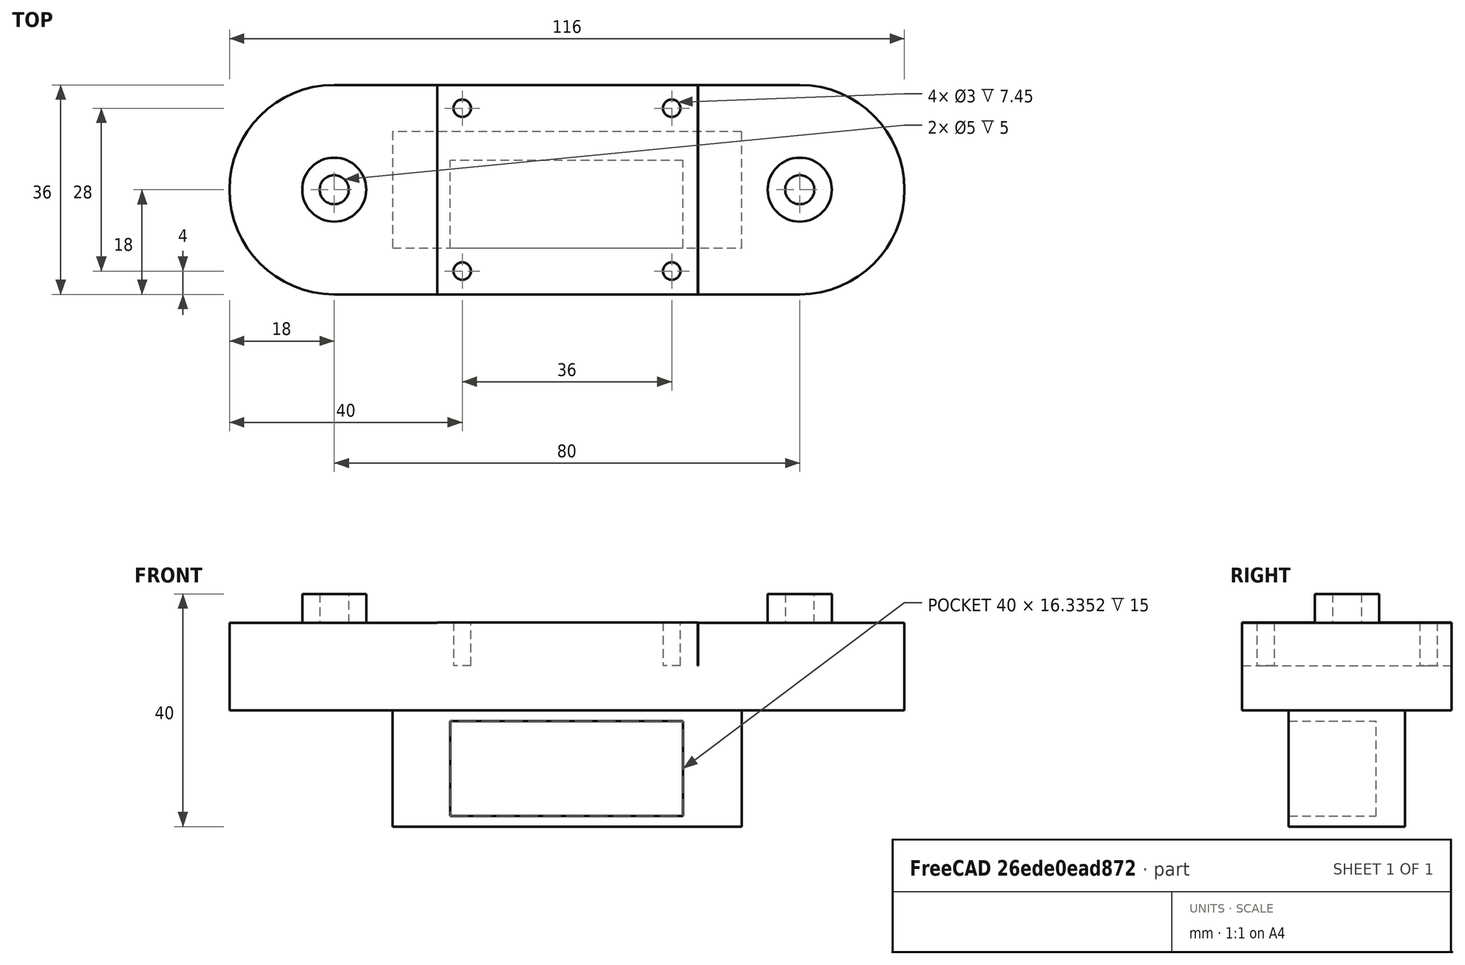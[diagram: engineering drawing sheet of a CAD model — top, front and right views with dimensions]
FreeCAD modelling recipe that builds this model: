
FCSTD DOCUMENT  (FreeCAD 0.19R24267 +148 (Git))
Label: Table
License: All rights reserved
LicenseURL: http://en.wikipedia.org/wiki/All_rights_reserved
objects: TechDraw::DrawViewDimension×64, Sketcher::SketchObject×7, PartDesign::Plane×5, TechDraw::DrawViewPart×5, PartDesign::Pad×4, PartDesign::Pocket×2, Part::Part2DObjectPython×1, PartDesign::Body×1, TechDraw::DrawSVGTemplate×1, TechDraw::DrawPage×1
note: 26 computed .brp shape members not serialized (recipe doc carries the construction recipe); baked Part::Feature solids carry a one-line shape summary decoded from their .brp

FEATURE [Sketcher::SketchObject] Sketch
  FullyConstrained = false
  MapMode = 5
  Support = -> [XY_Plane]
  sketch-geometry (16):
    g0: LineSegment StartX=-40 StartY=18 StartZ=0 EndX=40 EndY=18 EndZ=0
    g1: LineSegment StartX=40 StartY=-18 StartZ=0 EndX=-40 EndY=-18 EndZ=0
    g2: ArcOfCircle CenterX=-40 CenterY=-4.82e-14 CenterZ=0 NormalX=0 NormalY=0 NormalZ=1 AngleXU=0 Radius=18 StartAngle=1.5708 EndAngle=4.71239
    g3: ArcOfCircle CenterX=40 CenterY=-4.71e-14 CenterZ=0 NormalX=0 NormalY=0 NormalZ=1 AngleXU=0 Radius=18 StartAngle=4.71239 EndAngle=7.85398
    g4: LineSegment StartX=22.5 StartY=-18 StartZ=0 EndX=-22.5 EndY=-18 EndZ=0
    g5: LineSegment StartX=-22.5 StartY=-18 StartZ=0 EndX=-22.5 EndY=18 EndZ=0
    g6: LineSegment StartX=-22.5 StartY=18 StartZ=0 EndX=22.5 EndY=18 EndZ=0
    g7: LineSegment StartX=22.5 StartY=18 StartZ=0 EndX=22.5 EndY=-18 EndZ=0
    g8: Circle CenterX=-40 CenterY=-4.82e-14 CenterZ=0 NormalX=0 NormalY=0 NormalZ=1 AngleXU=0 Radius=10
    g9: Circle CenterX=40 CenterY=-4.71e-14 CenterZ=0 NormalX=0 NormalY=0 NormalZ=1 AngleXU=0 Radius=10
    g10: Circle CenterX=40 CenterY=-4.71e-14 CenterZ=0 NormalX=0 NormalY=0 NormalZ=1 AngleXU=0 Radius=5.5
    g11: Circle CenterX=-40 CenterY=-4.82e-14 CenterZ=0 NormalX=0 NormalY=0 NormalZ=1 AngleXU=0 Radius=5.5
    g12: Circle CenterX=-18 CenterY=14 CenterZ=0 NormalX=0 NormalY=0 NormalZ=1 AngleXU=0 Radius=1.5
    g13: Circle CenterX=18 CenterY=14 CenterZ=0 NormalX=0 NormalY=0 NormalZ=1 AngleXU=0 Radius=1.5
    g14: Circle CenterX=-18 CenterY=-14 CenterZ=0 NormalX=0 NormalY=0 NormalZ=1 AngleXU=0 Radius=1.5
    g15: Circle CenterX=18 CenterY=-14 CenterZ=0 NormalX=0 NormalY=0 NormalZ=1 AngleXU=0 Radius=1.5
  constraints (39):
    c: Horizontal(g0)
    c: Horizontal(g1)
    c: Symmetric(g0,g1,g-1)
    c: DistanceX(g0,g0) = 80
    c: Coincident(g4,g5)
    c: Coincident(g5,g6)
    c: Coincident(g6,g7)
    c: Coincident(g7,g4)
    c: Horizontal(g4)
    c: Horizontal(g6)
    c: Vertical(g5)
    c: Vertical(g7)
    c: PointOnObject(g4,g1)
    c: DistanceX(g5,g6) = 45
    c: Tangent(g2,g0) = 1.5708
    c: Symmetric(g5,g4,g-1)
    c: Coincident(g8,g2)
    c: Coincident(g9,g3)
    c: Coincident(g10,g3)
    c: Coincident(g11,g2)
    c: Diameter(g9) = 20
    c: Diameter(g10) = 11
    c: Diameter(g11) = 11
    c: Diameter(g8) = 20
    c: Tangent(g3,g0) = 1.5708
    c: Tangent(g1,g3)
    c: Tangent(g2,g1) = 1.5708
    c: Radius(g3) = 18
    c: Symmetric(g15,g12,g-1)
    c: DistanceX(g12,g13) = 36
    c: Equal(g13,g15)
    c: Diameter(g13) = 3
    c: Equal(g12,g14)
    c: Diameter(g12) = 3
    c: Vertical(g14,g12)
    c: Horizontal(g15,g14)
    c: Vertical(g13,g15)
    c: Horizontal(g13,g12)
    c: DistanceY(g14,g12) = 28
FEATURE [Sketcher::SketchObject] Sketch001  label="Top"
  ExternalGeometry = -> [Sketch]
  FullyConstrained = true
  MapMode = 5
  Support = -> [XY_Plane]
  sketch-geometry (4):
    g0: ArcOfCircle CenterX=-40 CenterY=0 CenterZ=0 NormalX=0 NormalY=0 NormalZ=1 AngleXU=0 Radius=18 StartAngle=1.5708 EndAngle=4.71239
    g1: ArcOfCircle CenterX=40 CenterY=0 CenterZ=0 NormalX=0 NormalY=0 NormalZ=1 AngleXU=0 Radius=18 StartAngle=4.71239 EndAngle=7.85398
    g2: LineSegment StartX=-40 StartY=18 StartZ=0 EndX=40 EndY=18 EndZ=0
    g3: LineSegment StartX=40 StartY=-18 StartZ=0 EndX=-40 EndY=-18 EndZ=0
  constraints (11):
    c: Coincident(g0,g-4)
    c: Coincident(g1,g-6)
    c: PointOnObject(g-6,g1)
    c: Coincident(g2,g-4)
    c: Coincident(g2,g-6)
    c: Coincident(g3,g-6)
    c: Coincident(g3,g-5)
    c: Coincident(g0,g2)
    c: Coincident(g0,g3)
    c: Coincident(g1,g3)
    c: Coincident(g1,g2)
FEATURE [Part::Part2DObjectPython] Clone2D  label="Sketch (2D)"  # Draft 2D object (typed FeaturePython)
  Fuse = false
  Objects = -> [Sketch]
  Placement = pos=(0,0,16) rot=(0,0,1;0rad)
  Scale = (1,1,1)
FEATURE [PartDesign::Pad] Pad
  Direction = (1,1,1)
  Length = 15
  Length2 = 100
  Profile = -> Sketch001
  Type = 0
FEATURE [PartDesign::Plane] DatumPlane
  Length = 130.952
  MapMode = 5
  Placement = pos=(0,-18,0) rot=(1,0,0;1.5708rad)
  ResizeMode = 0
  Support = -> [Pad]
  Width = 65.2143
FEATURE [Sketcher::SketchObject] Sketch002
  FullyConstrained = false
  MapMode = 5
  Placement = pos=(0,-18,0) rot=(1,0,0;1.5708rad)
  Support = -> [DatumPlane]
  sketch-geometry (4):
    g0: LineSegment StartX=-22.3088 StartY=31.7993 StartZ=0 EndX=22.546 EndY=31.7993 EndZ=0
    g1: LineSegment StartX=22.546 StartY=31.7993 StartZ=0 EndX=22.546 EndY=7.65691 EndZ=0
    g2: LineSegment StartX=22.546 StartY=7.65691 StartZ=0 EndX=-22.3088 EndY=7.65691 EndZ=0
    g3: LineSegment StartX=-22.3088 StartY=7.65691 StartZ=0 EndX=-22.3088 EndY=31.7993 EndZ=0
  constraints (8):
    c: Coincident(g0,g1)
    c: Coincident(g1,g2)
    c: Coincident(g2,g3)
    c: Coincident(g3,g0)
    c: Horizontal(g0)
    c: Horizontal(g2)
    c: Vertical(g1)
    c: Vertical(g3)
FEATURE [PartDesign::Pocket] Pocket
  BaseFeature = -> Pad
  Length = 36
  Length2 = 100
  Profile = -> Sketch002
  Type = 0
FEATURE [Sketcher::SketchObject] Sketch003
  ExternalGeometry = -> [Clone2D,Pocket]
  FullyConstrained = false
  MapMode = 5
  Placement = pos=(0,1.7e-15,7.65691) rot=(0,0,1;0rad)
  Support = -> [Pocket]
  sketch-geometry (8):
    g0: LineSegment StartX=-22.3088 StartY=18 StartZ=0 EndX=22.5 EndY=18 EndZ=0
    g1: LineSegment StartX=22.5 StartY=18 StartZ=0 EndX=22.5 EndY=-18 EndZ=0
    g2: LineSegment StartX=22.5 StartY=-18 StartZ=0 EndX=-22.3088 EndY=-18 EndZ=0
    g3: LineSegment StartX=-22.3088 StartY=-18 StartZ=0 EndX=-22.3088 EndY=18 EndZ=0
    g4: Circle CenterX=-18 CenterY=14 CenterZ=0 NormalX=0 NormalY=0 NormalZ=1 AngleXU=0 Radius=1.5
    g5: Circle CenterX=18 CenterY=14 CenterZ=0 NormalX=0 NormalY=0 NormalZ=1 AngleXU=0 Radius=1.5
    g6: Circle CenterX=18 CenterY=-14 CenterZ=0 NormalX=0 NormalY=0 NormalZ=1 AngleXU=0 Radius=1.5
    g7: Circle CenterX=-18 CenterY=-14 CenterZ=0 NormalX=0 NormalY=0 NormalZ=1 AngleXU=0 Radius=1.5
  constraints (14):
    c: Coincident(g0,g1)
    c: Coincident(g1,g2)
    c: Coincident(g2,g3)
    c: Coincident(g3,g0)
    c: Horizontal(g0)
    c: Horizontal(g2)
    c: Vertical(g1)
    c: Vertical(g3)
    c: Coincident(g0,g-4)
    c: Coincident(g1,g-5)
    c: Coincident(g4,g-7)
    c: Coincident(g5,g-9)
    c: Coincident(g6,g-10)
    c: Coincident(g7,g-8)
FEATURE [PartDesign::Plane] DatumPlane001
  Length = 130.952
  MapMode = 5
  Placement = pos=(0,1.7e-15,7.65691) rot=(0,0,1;0rad)
  ResizeMode = 0
  Support = -> [Pocket]
  Width = 65.2143
FEATURE [PartDesign::Pad] Pad001  label="Surface"
  BaseFeature = -> Pocket
  Direction = (1,1,1)
  Length = 7.45
  Length2 = 100
  Profile = -> Sketch003
  Type = 0
FEATURE [PartDesign::Plane] DatumPlane002
  Length = 130.952
  MapMode = 5
  Placement = pos=(0,0,15) rot=(0,0,1;0rad)
  ResizeMode = 0
  Support = -> [Pad001]
  Width = 65.2143
FEATURE [Sketcher::SketchObject] Sketch004
  ExternalGeometry = -> [Clone2D]
  FullyConstrained = false
  MapMode = 5
  Placement = pos=(0,0,15) rot=(0,0,1;0rad)
  Support = -> [Pad001]
  sketch-geometry (4):
    g0: Circle CenterX=-40 CenterY=-4.82e-14 CenterZ=0 NormalX=0 NormalY=0 NormalZ=1 AngleXU=0 Radius=2.5
    g1: Circle CenterX=40 CenterY=-4.71e-14 CenterZ=0 NormalX=0 NormalY=0 NormalZ=1 AngleXU=0 Radius=2.5
    g2: Circle CenterX=-40 CenterY=-4.82e-14 CenterZ=0 NormalX=0 NormalY=0 NormalZ=1 AngleXU=0 Radius=5.5
    g3: Circle CenterX=40 CenterY=-4.71e-14 CenterZ=0 NormalX=0 NormalY=0 NormalZ=1 AngleXU=0 Radius=5.5
  constraints (6):
    c: Coincident(g0,g-4)
    c: Coincident(g1,g-3)
    c: Coincident(g2,g0)
    c: Tangent(g2,g-4)
    c: Coincident(g3,g1)
    c: Tangent(g3,g-3)
FEATURE [PartDesign::Pad] Pad002
  BaseFeature = -> Pad001
  Direction = (1,1,1)
  Length = 5
  Length2 = 100
  Profile = -> Sketch004
  Type = 0
FEATURE [PartDesign::Plane] DatumPlane003
  Length = 130.952
  MapMode = 5
  Placement = pos=(0,0,0) rot=(1,0,0;3.14159rad)
  ResizeMode = 0
  Support = -> [Pad002]
  Width = 65.2143
FEATURE [Sketcher::SketchObject] Sketch005
  FullyConstrained = true
  MapMode = 5
  Placement = pos=(0,0,0) rot=(1,0,0;3.14159rad)
  Support = -> [Pad002]
  sketch-geometry (4):
    g0: LineSegment StartX=-30 StartY=10 StartZ=0 EndX=30 EndY=10 EndZ=0
    g1: LineSegment StartX=30 StartY=10 StartZ=0 EndX=30 EndY=-10 EndZ=0
    g2: LineSegment StartX=30 StartY=-10 StartZ=0 EndX=-30 EndY=-10 EndZ=0
    g3: LineSegment StartX=-30 StartY=-10 StartZ=0 EndX=-30 EndY=10 EndZ=0
  constraints (11):
    c: Coincident(g0,g1)
    c: Coincident(g1,g2)
    c: Coincident(g2,g3)
    c: Coincident(g3,g0)
    c: Horizontal(g0)
    c: Horizontal(g2)
    c: Vertical(g1)
    c: Vertical(g3)
    c: Symmetric(g1,g0,g-1)
    c: DistanceX(g0,g0) = 60
    c: DistanceY(g3,g3) = 20
FEATURE [PartDesign::Pad] Pad003  label="Base"
  BaseFeature = -> Pad002
  Direction = (1,1,1)
  Length = 20
  Length2 = 100
  Profile = -> Sketch005
  Type = 0
FEATURE [PartDesign::Plane] DatumPlane004
  Length = 130.952
  MapMode = 5
  Placement = pos=(0,-10,0) rot=(1,0,0;1.5708rad)
  ResizeMode = 0
  Support = -> [Pad003]
  Width = 65.2143
FEATURE [Sketcher::SketchObject] Sketch006
  FullyConstrained = false
  MapMode = 5
  Placement = pos=(0,-10,0) rot=(1,0,0;1.5708rad)
  Support = -> [Pad003]
  sketch-geometry (4):
    g0: LineSegment StartX=-20.0443 StartY=-1.87066 StartZ=0 EndX=19.9557 EndY=-1.87066 EndZ=0
    g1: LineSegment StartX=19.9557 StartY=-1.87066 StartZ=0 EndX=19.9557 EndY=-18.2059 EndZ=0
    g2: LineSegment StartX=19.9557 StartY=-18.2059 StartZ=0 EndX=-20.0443 EndY=-18.2059 EndZ=0
    g3: LineSegment StartX=-20.0443 StartY=-18.2059 StartZ=0 EndX=-20.0443 EndY=-1.87066 EndZ=0
  constraints (9):
    c: Coincident(g0,g1)
    c: Coincident(g1,g2)
    c: Coincident(g2,g3)
    c: Coincident(g3,g0)
    c: Horizontal(g0)
    c: Horizontal(g2)
    c: Vertical(g1)
    c: Vertical(g3)
    c: DistanceX(g0,g0) = 40
FEATURE [PartDesign::Pocket] Pocket001  label="Foot area"
  BaseFeature = -> Pad003
  Length = 15
  Length2 = 100
  Profile = -> Sketch006
  Type = 0
FEATURE [PartDesign::Body] Body
  Group = -> [Sketch,Sketch001,Clone2D,Pad,DatumPlane,Sketch002,Pocket,Sketch003,DatumPlane001,Pad001,DatumPlane002,Sketch004,Pad002,DatumPlane003,Sketch005,Pad003,DatumPlane004,Sketch006,Pocket001]
  Origin = -> Origin
  Tip = -> Pocket001
FEATURE [TechDraw::DrawSVGTemplate] Template
  EditableTexts = AuthorName=AUTHOR NAME; CheckDate=CHECK DATE; CreationDate=CREATION DATE; DrawingNumber=NUMBER; FC-Scale=SCALE; FC-Title=TITLE; SheetNumber=SHEET; Subtitle=SUBTITLE; SupervisorName=SUPERVISOR NAME; Weight=WEIGHT
  Height = 297
  Orientation = 1
  Width = 420
FEATURE [TechDraw::DrawViewPart] View  label="TOP VIEW"
  CoarseView = false
  Direction = (0,0,1)
  Focus = 100
  HardHidden = false
  IsoCount = 0
  IsoHidden = false
  IsoVisible = false
  LockPosition = false
  Perspective = false
  Rotation = 0
  ScaleType = 0
  SeamHidden = false
  SeamVisible = true
  SmoothHidden = false
  SmoothVisible = true
  Source = -> [Pocket001]
  X = 106.209
  XDirection = (1,0,0)
  Y = 222.175
FEATURE [TechDraw::DrawViewPart] View002  label="SIDE VIEW"
  CoarseView = false
  Direction = (-1,0,0)
  Focus = 100
  HardHidden = false
  IsoCount = 0
  IsoHidden = false
  IsoVisible = false
  LockPosition = false
  Perspective = false
  Rotation = 0
  ScaleType = 0
  SeamHidden = false
  SeamVisible = true
  SmoothHidden = false
  SmoothVisible = true
  Source = -> [Pocket001]
  X = 116.97
  XDirection = (0,-1,0)
  Y = 51.7602
FEATURE [TechDraw::DrawViewPart] View004  label="FRONT VIEW"
  CoarseView = false
  Direction = (0,-1,0)
  Focus = 100
  HardHidden = false
  IsoCount = 0
  IsoHidden = false
  IsoVisible = false
  LockPosition = false
  Perspective = false
  Rotation = 0
  ScaleType = 0
  SeamHidden = false
  SeamVisible = true
  SmoothHidden = false
  SmoothVisible = true
  Source = -> [Pocket001]
  X = 310.217
  XDirection = (1,0,0)
  Y = 223.753
FEATURE [TechDraw::DrawViewPart] View005  label="REAR VIEW"
  CoarseView = false
  Direction = (0,1,0)
  Focus = 100
  HardHidden = false
  IsoCount = 0
  IsoHidden = false
  IsoVisible = false
  LockPosition = false
  Perspective = false
  Rotation = 0
  ScaleType = 0
  SeamHidden = false
  SeamVisible = true
  SmoothHidden = false
  SmoothVisible = true
  Source = -> [Pocket001]
  X = 109.362
  XDirection = (-1,0,0)
  Y = 142.933
FEATURE [TechDraw::DrawViewDimension] Dimension
  Arbitrary = false
  ArbitraryTolerances = false
  EqualTolerance = true
  FormatSpec = R%.2f
  FormatSpecOverTolerance = %+.2f
  FormatSpecUnderTolerance = %+.2f
  Inverted = false
  LockPosition = false
  MeasureType = 1
  OverTolerance = 0
  References2D = -> [View]
  Rotation = 0
  ScaleType = 0
  TheoreticalExact = false
  Type = 4
  UnderTolerance = 0
  X = -71.6753
  Y = 37.6599
FEATURE [TechDraw::DrawViewDimension] Dimension001
  Arbitrary = false
  ArbitraryTolerances = false
  EqualTolerance = true
  FormatSpec = R%.2f
  FormatSpecOverTolerance = %+.2f
  FormatSpecUnderTolerance = %+.2f
  Inverted = false
  LockPosition = false
  MeasureType = 1
  OverTolerance = 0
  References2D = -> [View]
  Rotation = 0
  ScaleType = 0
  TheoreticalExact = false
  Type = 4
  UnderTolerance = 0
  X = 64.3863
  Y = 31.8894
FEATURE [TechDraw::DrawViewDimension] Dimension002
  Arbitrary = false
  ArbitraryTolerances = false
  EqualTolerance = true
  FormatSpec = ⌀%.2f
  FormatSpecOverTolerance = %+.2f
  FormatSpecUnderTolerance = %+.2f
  Inverted = false
  LockPosition = false
  MeasureType = 1
  OverTolerance = 0
  References2D = -> [View]
  Rotation = 0
  ScaleType = 0
  TheoreticalExact = false
  Type = 5
  UnderTolerance = 0
  X = -75.9273
  Y = 22.4745
FEATURE [TechDraw::DrawViewDimension] Dimension004
  Arbitrary = false
  ArbitraryTolerances = false
  EqualTolerance = true
  FormatSpec = ⌀%.2f
  FormatSpecOverTolerance = %+.2f
  FormatSpecUnderTolerance = %+.2f
  Inverted = false
  LockPosition = false
  MeasureType = 1
  OverTolerance = 0
  References2D = -> [View]
  Rotation = 0
  ScaleType = 0
  TheoreticalExact = false
  Type = 5
  UnderTolerance = 0
  X = 85.5542
  Y = 25.1809
FEATURE [TechDraw::DrawViewDimension] Dimension006
  Arbitrary = false
  ArbitraryTolerances = false
  EqualTolerance = true
  FormatSpec = ⌀%.2f
  FormatSpecOverTolerance = %+.2f
  FormatSpecUnderTolerance = %+.2f
  Inverted = false
  LockPosition = false
  MeasureType = 1
  OverTolerance = 0
  References2D = -> [View]
  Rotation = 0
  ScaleType = 0
  TheoreticalExact = false
  Type = 5
  UnderTolerance = 0
  X = -8.27891
  Y = 7.31624
FEATURE [TechDraw::DrawViewDimension] Dimension007
  Arbitrary = false
  ArbitraryTolerances = false
  EqualTolerance = true
  FormatSpec = ⌀%.2f
  FormatSpecOverTolerance = %+.2f
  FormatSpecUnderTolerance = %+.2f
  Inverted = false
  LockPosition = false
  MeasureType = 1
  OverTolerance = 0
  References2D = -> [View]
  Rotation = 0
  ScaleType = 0
  TheoreticalExact = false
  Type = 5
  UnderTolerance = 0
  X = 3.65812
  Y = 5.19838
FEATURE [TechDraw::DrawViewDimension] Dimension008
  Arbitrary = false
  ArbitraryTolerances = false
  EqualTolerance = true
  FormatSpec = ⌀%.2f
  FormatSpecOverTolerance = %+.2f
  FormatSpecUnderTolerance = %+.2f
  Inverted = false
  LockPosition = false
  MeasureType = 1
  OverTolerance = 0
  References2D = -> [View]
  Rotation = 0
  ScaleType = 0
  TheoreticalExact = false
  Type = 5
  UnderTolerance = 0
  X = 5.77598
  Y = -8.27891
FEATURE [TechDraw::DrawViewDimension] Dimension009
  Arbitrary = false
  ArbitraryTolerances = false
  EqualTolerance = true
  FormatSpec = ⌀%.2f
  FormatSpecOverTolerance = %+.2f
  FormatSpecUnderTolerance = %+.2f
  Inverted = false
  LockPosition = false
  MeasureType = 1
  OverTolerance = 0
  References2D = -> [View]
  Rotation = 0
  ScaleType = 0
  TheoreticalExact = false
  Type = 5
  UnderTolerance = 0
  X = -7.70131
  Y = -5.77598
FEATURE [TechDraw::DrawViewDimension] Dimension010
  Arbitrary = false
  ArbitraryTolerances = false
  EqualTolerance = true
  FormatSpec = %.2f
  FormatSpecOverTolerance = %+.2f
  FormatSpecUnderTolerance = %+.2f
  Inverted = false
  LockPosition = false
  MeasureType = 1
  OverTolerance = 0
  References2D = -> [View]
  Rotation = 0
  ScaleType = 0
  TheoreticalExact = false
  Type = 1
  UnderTolerance = 0
  X = -1.3335
  Y = 46.9068
FEATURE [TechDraw::DrawViewDimension] Dimension011
  Arbitrary = false
  ArbitraryTolerances = false
  EqualTolerance = true
  FormatSpec = %.2f
  FormatSpecOverTolerance = %+.2f
  FormatSpecUnderTolerance = %+.2f
  Inverted = false
  LockPosition = false
  MeasureType = 1
  OverTolerance = 0
  References2D = -> [View]
  Rotation = 0
  ScaleType = 0
  TheoreticalExact = false
  Type = 2
  UnderTolerance = 0
  X = -29.24
  Y = 28.3023
FEATURE [TechDraw::DrawViewDimension] Dimension012
  Arbitrary = false
  ArbitraryTolerances = false
  EqualTolerance = true
  FormatSpec = ⌀%.2f
  FormatSpecOverTolerance = %+.2f
  FormatSpecUnderTolerance = %+.2f
  Inverted = false
  LockPosition = false
  MeasureType = 1
  OverTolerance = 0
  References2D = -> [View]
  Rotation = 0
  ScaleType = 0
  TheoreticalExact = false
  Type = 5
  UnderTolerance = 0
  X = 73.1939
  Y = -17.9188
FEATURE [TechDraw::DrawViewDimension] Dimension013
  Arbitrary = false
  ArbitraryTolerances = false
  EqualTolerance = true
  FormatSpec = ⌀%.2f
  FormatSpecOverTolerance = %+.2f
  FormatSpecUnderTolerance = %+.2f
  Inverted = false
  LockPosition = false
  MeasureType = 1
  OverTolerance = 0
  References2D = -> [View]
  Rotation = 0
  ScaleType = 0
  TheoreticalExact = false
  Type = 5
  UnderTolerance = 0
  X = 0
  Y = 0
FEATURE [TechDraw::DrawViewDimension] Dimension014
  Arbitrary = false
  ArbitraryTolerances = false
  EqualTolerance = true
  FormatSpec = ⌀%.2f
  FormatSpecOverTolerance = %+.2f
  FormatSpecUnderTolerance = %+.2f
  Inverted = false
  LockPosition = false
  MeasureType = 1
  OverTolerance = 0
  References2D = -> [View]
  Rotation = 0
  ScaleType = 0
  TheoreticalExact = false
  Type = 5
  UnderTolerance = 0
  X = -70.1568
  Y = -20.0448
FEATURE [TechDraw::DrawViewDimension] Dimension015
  Arbitrary = false
  ArbitraryTolerances = false
  EqualTolerance = true
  FormatSpec = %.2f
  FormatSpecOverTolerance = %+.2f
  FormatSpecUnderTolerance = %+.2f
  Inverted = false
  LockPosition = false
  MeasureType = 1
  OverTolerance = 0
  References2D = -> [View]
  Rotation = 0
  ScaleType = 0
  TheoreticalExact = false
  Type = 1
  UnderTolerance = 0
  X = -0.303709
  Y = 56.0215
FEATURE [TechDraw::DrawViewDimension] Dimension016
  Arbitrary = false
  ArbitraryTolerances = false
  EqualTolerance = true
  FormatSpec = %.2f
  FormatSpecOverTolerance = %+.2f
  FormatSpecUnderTolerance = %+.2f
  Inverted = false
  LockPosition = false
  MeasureType = 1
  OverTolerance = 0
  References2D = -> [View002]
  Rotation = 0
  ScaleType = 0
  TheoreticalExact = false
  Type = 6
  UnderTolerance = 0
  X = -7.80819
  Y = 10.3801
FEATURE [TechDraw::DrawViewDimension] Dimension017
  Arbitrary = false
  ArbitraryTolerances = false
  EqualTolerance = true
  FormatSpec = %.2f
  FormatSpecOverTolerance = %+.2f
  FormatSpecUnderTolerance = %+.2f
  Inverted = false
  LockPosition = false
  MeasureType = 1
  OverTolerance = 0
  References2D = -> [View002]
  Rotation = 0
  ScaleType = 0
  TheoreticalExact = false
  Type = 2
  UnderTolerance = 0
  X = -44.2259
  Y = 51.8343
FEATURE [TechDraw::DrawViewDimension] Dimension018
  Arbitrary = false
  ArbitraryTolerances = false
  EqualTolerance = true
  FormatSpec = %.2f
  FormatSpecOverTolerance = %+.2f
  FormatSpecUnderTolerance = %+.2f
  Inverted = false
  LockPosition = false
  MeasureType = 1
  OverTolerance = 0
  References2D = -> [View002]
  Rotation = 0
  ScaleType = 0
  TheoreticalExact = false
  Type = 1
  UnderTolerance = 0
  X = 27.5473
  Y = 58.3266
FEATURE [TechDraw::DrawViewDimension] Dimension019
  Arbitrary = false
  ArbitraryTolerances = false
  EqualTolerance = true
  FormatSpec = %.2f
  FormatSpecOverTolerance = %+.2f
  FormatSpecUnderTolerance = %+.2f
  Inverted = false
  LockPosition = false
  MeasureType = 1
  OverTolerance = 0
  References2D = -> [View002]
  Rotation = 0
  ScaleType = 0
  TheoreticalExact = false
  Type = 1
  UnderTolerance = 0
  X = -38.7259
  Y = -9.22063
FEATURE [TechDraw::DrawViewDimension] Dimension021
  Arbitrary = false
  ArbitraryTolerances = false
  EqualTolerance = true
  FormatSpec = %.2f
  FormatSpecOverTolerance = %+.2f
  FormatSpecUnderTolerance = %+.2f
  Inverted = false
  LockPosition = false
  MeasureType = 1
  OverTolerance = 0
  References2D = -> [View002]
  Rotation = 0
  ScaleType = 0
  TheoreticalExact = false
  Type = 2
  UnderTolerance = 0
  X = 39.1595
  Y = 40.2373
FEATURE [TechDraw::DrawViewDimension] Dimension022
  Arbitrary = false
  ArbitraryTolerances = false
  EqualTolerance = true
  FormatSpec = %.2f
  FormatSpecOverTolerance = %+.2f
  FormatSpecUnderTolerance = %+.2f
  Inverted = false
  LockPosition = false
  MeasureType = 1
  OverTolerance = 0
  References2D = -> [View002]
  Rotation = 0
  ScaleType = 0
  TheoreticalExact = false
  Type = 1
  UnderTolerance = 0
  X = 23.7271
  Y = 45.8481
FEATURE [TechDraw::DrawViewDimension] Dimension023
  Arbitrary = false
  ArbitraryTolerances = false
  EqualTolerance = true
  FormatSpec = %.2f
  FormatSpecOverTolerance = %+.2f
  FormatSpecUnderTolerance = %+.2f
  Inverted = false
  LockPosition = false
  MeasureType = 1
  OverTolerance = 0
  References2D = -> [View002]
  Rotation = 0
  ScaleType = 0
  TheoreticalExact = false
  Type = 1
  UnderTolerance = 0
  X = -84.638
  Y = 2.39541
FEATURE [TechDraw::DrawViewDimension] Dimension024
  Arbitrary = false
  ArbitraryTolerances = false
  EqualTolerance = true
  FormatSpec = %.2f
  FormatSpecOverTolerance = %+.2f
  FormatSpecUnderTolerance = %+.2f
  Inverted = false
  LockPosition = false
  MeasureType = 1
  OverTolerance = 0
  References2D = -> [View005]
  Rotation = 0
  ScaleType = 0
  TheoreticalExact = false
  Type = 1
  UnderTolerance = 0
  X = -0.89406
  Y = 39.4603
FEATURE [TechDraw::DrawViewDimension] Dimension025
  Arbitrary = false
  ArbitraryTolerances = false
  EqualTolerance = true
  FormatSpec = %.2f
  FormatSpecOverTolerance = %+.2f
  FormatSpecUnderTolerance = %+.2f
  Inverted = false
  LockPosition = false
  MeasureType = 1
  OverTolerance = 0
  References2D = -> [View005]
  Rotation = 0
  ScaleType = 0
  TheoreticalExact = false
  Type = 1
  UnderTolerance = 0
  X = -4.00916
  Y = 48.8136
FEATURE [TechDraw::DrawViewDimension] Dimension026
  Arbitrary = false
  ArbitraryTolerances = false
  EqualTolerance = true
  FormatSpec = %.2f
  FormatSpecOverTolerance = %+.2f
  FormatSpecUnderTolerance = %+.2f
  Inverted = false
  LockPosition = false
  MeasureType = 1
  OverTolerance = 0
  References2D = -> [View005]
  Rotation = 0
  ScaleType = 0
  TheoreticalExact = false
  Type = 1
  UnderTolerance = 0
  X = -67.5473
  Y = 45.1519
FEATURE [TechDraw::DrawViewDimension] Dimension027
  Arbitrary = false
  ArbitraryTolerances = false
  EqualTolerance = true
  FormatSpec = %.2f
  FormatSpecOverTolerance = %+.2f
  FormatSpecUnderTolerance = %+.2f
  Inverted = false
  LockPosition = false
  MeasureType = 1
  OverTolerance = 0
  References2D = -> [View005]
  Rotation = 0
  ScaleType = 0
  TheoreticalExact = false
  Type = 1
  UnderTolerance = 0
  X = 63.9542
  Y = 42.3572
FEATURE [TechDraw::DrawViewDimension] Dimension028
  Arbitrary = false
  ArbitraryTolerances = false
  EqualTolerance = true
  FormatSpec = %.2f
  FormatSpecOverTolerance = %+.2f
  FormatSpecUnderTolerance = %+.2f
  Inverted = false
  LockPosition = false
  MeasureType = 1
  OverTolerance = 0
  References2D = -> [View005]
  Rotation = 0
  ScaleType = 0
  TheoreticalExact = false
  Type = 2
  UnderTolerance = 0
  X = -74.0014
  Y = -20.557
FEATURE [TechDraw::DrawViewDimension] Dimension029
  Arbitrary = false
  ArbitraryTolerances = false
  EqualTolerance = true
  FormatSpec = %.2f
  FormatSpecOverTolerance = %+.2f
  FormatSpecUnderTolerance = %+.2f
  Inverted = false
  LockPosition = false
  MeasureType = 1
  OverTolerance = 0
  References2D = -> [View005]
  Rotation = 0
  ScaleType = 0
  TheoreticalExact = false
  Type = 1
  UnderTolerance = 0
  X = -46.6046
  Y = -5.36103
FEATURE [TechDraw::DrawViewDimension] Dimension030
  Arbitrary = false
  ArbitraryTolerances = false
  EqualTolerance = true
  FormatSpec = %.2f
  FormatSpecOverTolerance = %+.2f
  FormatSpecUnderTolerance = %+.2f
  Inverted = false
  LockPosition = false
  MeasureType = 1
  OverTolerance = 0
  References2D = -> [View005]
  Rotation = 0
  ScaleType = 0
  TheoreticalExact = false
  Type = 1
  UnderTolerance = 0
  X = 47.4031
  Y = -4.16332
FEATURE [TechDraw::DrawViewDimension] Dimension031
  Arbitrary = false
  ArbitraryTolerances = false
  EqualTolerance = true
  FormatSpec = %.2f
  FormatSpecOverTolerance = %+.2f
  FormatSpecUnderTolerance = %+.2f
  Inverted = false
  LockPosition = false
  MeasureType = 1
  OverTolerance = 0
  References2D = -> [View005]
  Rotation = 0
  ScaleType = 0
  TheoreticalExact = false
  Type = 0
  UnderTolerance = 0
  X = 78.898
  Y = 25.4847
FEATURE [TechDraw::DrawViewDimension] Dimension032
  Arbitrary = false
  ArbitraryTolerances = false
  EqualTolerance = true
  FormatSpec = %.2f
  FormatSpecOverTolerance = %+.2f
  FormatSpecUnderTolerance = %+.2f
  Inverted = false
  LockPosition = false
  MeasureType = 1
  OverTolerance = 0
  References2D = -> [View005]
  Rotation = 0
  ScaleType = 0
  TheoreticalExact = false
  Type = 0
  UnderTolerance = 0
  X = -79.2973
  Y = 31.074
FEATURE [TechDraw::DrawViewDimension] Dimension033
  Arbitrary = false
  ArbitraryTolerances = false
  EqualTolerance = true
  FormatSpec = %.2f
  FormatSpecOverTolerance = %+.2f
  FormatSpecUnderTolerance = %+.2f
  Inverted = false
  LockPosition = false
  MeasureType = 1
  OverTolerance = 0
  References2D = -> [View005]
  Rotation = 0
  ScaleType = 0
  TheoreticalExact = false
  Type = 1
  UnderTolerance = 0
  X = -1.59694
  Y = -6.02675
FEATURE [TechDraw::DrawViewDimension] Dimension034
  Arbitrary = false
  ArbitraryTolerances = false
  EqualTolerance = true
  FormatSpec = %.2f
  FormatSpecOverTolerance = %+.2f
  FormatSpecUnderTolerance = %+.2f
  Inverted = false
  LockPosition = false
  MeasureType = 1
  OverTolerance = 0
  References2D = -> [View004]
  Rotation = 0
  ScaleType = 0
  TheoreticalExact = false
  Type = 1
  UnderTolerance = 0
  X = -41.4372
  Y = 36.2888
FEATURE [TechDraw::DrawViewDimension] Dimension035
  Arbitrary = false
  ArbitraryTolerances = false
  EqualTolerance = true
  FormatSpec = %.2f
  FormatSpecOverTolerance = %+.2f
  FormatSpecUnderTolerance = %+.2f
  Inverted = false
  LockPosition = false
  MeasureType = 1
  OverTolerance = 0
  References2D = -> [View004]
  Rotation = 0
  ScaleType = 0
  TheoreticalExact = false
  Type = 1
  UnderTolerance = 0
  X = 37.6046
  Y = 33.4143
FEATURE [TechDraw::DrawViewDimension] Dimension036
  Arbitrary = false
  ArbitraryTolerances = false
  EqualTolerance = true
  FormatSpec = %.2f
  FormatSpecOverTolerance = %+.2f
  FormatSpecUnderTolerance = %+.2f
  Inverted = false
  LockPosition = false
  MeasureType = 1
  OverTolerance = 0
  References2D = -> [View004]
  Rotation = 0
  ScaleType = 0
  TheoreticalExact = false
  Type = 1
  UnderTolerance = 0
  X = -0.383495
  Y = 34.7493
FEATURE [TechDraw::DrawViewDimension] Dimension037
  Arbitrary = false
  ArbitraryTolerances = false
  EqualTolerance = true
  FormatSpec = %.2f
  FormatSpecOverTolerance = %+.2f
  FormatSpecUnderTolerance = %+.2f
  Inverted = false
  LockPosition = false
  MeasureType = 1
  OverTolerance = 0
  References2D = -> [View004]
  Rotation = 0
  ScaleType = 0
  TheoreticalExact = false
  Type = 1
  UnderTolerance = 0
  X = -31.1544
  Y = 45.1822
FEATURE [TechDraw::DrawViewDimension] Dimension038
  Arbitrary = false
  ArbitraryTolerances = false
  EqualTolerance = true
  FormatSpec = %.2f
  FormatSpecOverTolerance = %+.2f
  FormatSpecUnderTolerance = %+.2f
  Inverted = false
  LockPosition = false
  MeasureType = 1
  OverTolerance = 0
  References2D = -> [View004]
  Rotation = 0
  ScaleType = 0
  TheoreticalExact = false
  Type = 1
  UnderTolerance = 0
  X = 32.7102
  Y = 44.7031
FEATURE [TechDraw::DrawViewDimension] Dimension039
  Arbitrary = false
  ArbitraryTolerances = false
  EqualTolerance = true
  FormatSpec = %.2f
  FormatSpecOverTolerance = %+.2f
  FormatSpecUnderTolerance = %+.2f
  Inverted = false
  LockPosition = false
  MeasureType = 1
  OverTolerance = 0
  References2D = -> [View004]
  Rotation = 0
  ScaleType = 0
  TheoreticalExact = false
  Type = 2
  UnderTolerance = 0
  X = -72.3725
  Y = 8.45817
FEATURE [TechDraw::DrawViewDimension] Dimension040
  Arbitrary = false
  ArbitraryTolerances = false
  EqualTolerance = true
  FormatSpec = %.2f
  FormatSpecOverTolerance = %+.2f
  FormatSpecUnderTolerance = %+.2f
  Inverted = false
  LockPosition = false
  MeasureType = 1
  OverTolerance = 0
  References2D = -> [View004]
  Rotation = 0
  ScaleType = 0
  TheoreticalExact = false
  Type = 2
  UnderTolerance = 0
  X = 70.4562
  Y = 8.45817
FEATURE [TechDraw::DrawViewDimension] Dimension041
  Arbitrary = false
  ArbitraryTolerances = false
  EqualTolerance = true
  FormatSpec = %.2f
  FormatSpecOverTolerance = %+.2f
  FormatSpecUnderTolerance = %+.2f
  Inverted = false
  LockPosition = false
  MeasureType = 1
  OverTolerance = 0
  References2D = -> [View004]
  Rotation = 0
  ScaleType = 0
  TheoreticalExact = false
  Type = 1
  UnderTolerance = 0
  X = -0.958166
  Y = 51.741
FEATURE [TechDraw::DrawViewDimension] Dimension042
  Arbitrary = false
  ArbitraryTolerances = false
  EqualTolerance = true
  FormatSpec = %.2f
  FormatSpecOverTolerance = %+.2f
  FormatSpecUnderTolerance = %+.2f
  Inverted = false
  LockPosition = false
  MeasureType = 1
  OverTolerance = 0
  References2D = -> [View004]
  Rotation = 0
  ScaleType = 0
  TheoreticalExact = false
  Type = 1
  UnderTolerance = 0
  X = -49
  Y = 0
FEATURE [TechDraw::DrawViewDimension] Dimension043
  Arbitrary = false
  ArbitraryTolerances = false
  EqualTolerance = true
  FormatSpec = %.2f
  FormatSpecOverTolerance = %+.2f
  FormatSpecUnderTolerance = %+.2f
  Inverted = false
  LockPosition = false
  MeasureType = 1
  OverTolerance = 0
  References2D = -> [View004]
  Rotation = 0
  ScaleType = 0
  TheoreticalExact = false
  Type = 1
  UnderTolerance = 0
  X = 49
  Y = 0
FEATURE [TechDraw::DrawViewDimension] Dimension044
  Arbitrary = false
  ArbitraryTolerances = false
  EqualTolerance = true
  FormatSpec = %.2f
  FormatSpecOverTolerance = %+.2f
  FormatSpecUnderTolerance = %+.2f
  Inverted = false
  LockPosition = false
  MeasureType = 1
  OverTolerance = 0
  References2D = -> [View004]
  Rotation = 0
  ScaleType = 0
  TheoreticalExact = false
  Type = 2
  UnderTolerance = 0
  X = -43.4143
  Y = -19.1026
FEATURE [TechDraw::DrawViewDimension] Dimension045
  Arbitrary = false
  ArbitraryTolerances = false
  EqualTolerance = true
  FormatSpec = %.2f
  FormatSpecOverTolerance = %+.2f
  FormatSpecUnderTolerance = %+.2f
  Inverted = false
  LockPosition = false
  MeasureType = 1
  OverTolerance = 0
  References2D = -> [View004]
  Rotation = 0
  ScaleType = 0
  TheoreticalExact = false
  Type = 1
  UnderTolerance = 0
  X = 3.83266
  Y = -3.71118
FEATURE [TechDraw::DrawViewDimension] Dimension046
  Arbitrary = false
  ArbitraryTolerances = false
  EqualTolerance = true
  FormatSpec = %.2f
  FormatSpecOverTolerance = %+.2f
  FormatSpecUnderTolerance = %+.2f
  Inverted = false
  LockPosition = false
  MeasureType = 1
  OverTolerance = 0
  References2D = -> [View004]
  Rotation = 0
  ScaleType = 0
  TheoreticalExact = false
  Type = 1
  UnderTolerance = 0
  X = -1.96064
  Y = -10.5406
FEATURE [TechDraw::DrawViewPart] View003  label="ISOMETRIC VIEW"
  CoarseView = false
  Direction = (0.577,-0.577,0.577)
  Focus = 100
  HardHidden = false
  IsoCount = 0
  IsoHidden = false
  IsoVisible = false
  LockPosition = false
  Perspective = false
  Rotation = 0
  ScaleType = 0
  SeamHidden = false
  SeamVisible = true
  SmoothHidden = false
  SmoothVisible = true
  Source = -> [Pocket001]
  X = 318.957
  XDirection = (0.707,0.707,0)
  Y = 129.042
FEATURE [TechDraw::DrawViewDimension] Dimension048
  Arbitrary = false
  ArbitraryTolerances = false
  EqualTolerance = true
  FormatSpec = ⌀%.2f
  FormatSpecOverTolerance = %+.2f
  FormatSpecUnderTolerance = %+.2f
  Inverted = false
  LockPosition = false
  MeasureType = 1
  OverTolerance = 0
  References2D = -> [View003]
  Rotation = 0
  ScaleType = 0
  TheoreticalExact = false
  Type = 5
  UnderTolerance = 0
  X = -97.0143
  Y = 55.893
FEATURE [TechDraw::DrawViewDimension] Dimension047
  Arbitrary = false
  ArbitraryTolerances = false
  EqualTolerance = true
  FormatSpec = R%.2f
  FormatSpecOverTolerance = %+.2f
  FormatSpecUnderTolerance = %+.2f
  Inverted = false
  LockPosition = false
  MeasureType = 1
  OverTolerance = 0
  References2D = -> [View003]
  Rotation = 0
  ScaleType = 0
  TheoreticalExact = false
  Type = 4
  UnderTolerance = 0
  X = -94.6003
  Y = 38.9574
FEATURE [TechDraw::DrawViewDimension] Dimension056
  Arbitrary = false
  ArbitraryTolerances = false
  EqualTolerance = true
  FormatSpec = ⌀%.2f
  FormatSpecOverTolerance = %+.2f
  FormatSpecUnderTolerance = %+.2f
  Inverted = false
  LockPosition = false
  MeasureType = 1
  OverTolerance = 0
  References2D = -> [View003]
  Rotation = 0
  ScaleType = 0
  TheoreticalExact = false
  Type = 5
  UnderTolerance = 0
  X = 77.1856
  Y = 13.3079
FEATURE [TechDraw::DrawViewDimension] Dimension054
  Arbitrary = false
  ArbitraryTolerances = false
  EqualTolerance = true
  FormatSpec = R%.2f
  FormatSpecOverTolerance = %+.2f
  FormatSpecUnderTolerance = %+.2f
  Inverted = false
  LockPosition = false
  MeasureType = 1
  OverTolerance = 0
  References2D = -> [View003]
  Rotation = 0
  ScaleType = 0
  TheoreticalExact = false
  Type = 4
  UnderTolerance = 0
  X = -69.8663
  Y = -8.98281
FEATURE [TechDraw::DrawViewDimension] Dimension058
  Arbitrary = false
  ArbitraryTolerances = false
  EqualTolerance = true
  FormatSpec = ⌀%.2f
  FormatSpecOverTolerance = %+.2f
  FormatSpecUnderTolerance = %+.2f
  Inverted = false
  LockPosition = false
  MeasureType = 1
  OverTolerance = 0
  References2D = -> [View003]
  Rotation = 0
  ScaleType = 0
  TheoreticalExact = false
  Type = 5
  UnderTolerance = 0
  X = 75.5221
  Y = 27.6138
FEATURE [TechDraw::DrawViewDimension] Dimension050
  Arbitrary = false
  ArbitraryTolerances = false
  EqualTolerance = true
  FormatSpec = %.2f
  FormatSpecOverTolerance = %+.2f
  FormatSpecUnderTolerance = %+.2f
  Inverted = false
  LockPosition = false
  MeasureType = 1
  OverTolerance = 0
  References2D = -> [View003]
  Rotation = 0
  ScaleType = 0
  TheoreticalExact = false
  Type = 1
  UnderTolerance = 0
  X = 54.17
  Y = 33.2639
FEATURE [TechDraw::DrawViewDimension] Dimension053
  Arbitrary = false
  ArbitraryTolerances = false
  EqualTolerance = true
  FormatSpec = %.2f
  FormatSpecOverTolerance = %+.2f
  FormatSpecUnderTolerance = %+.2f
  Inverted = false
  LockPosition = false
  MeasureType = 1
  OverTolerance = 0
  References2D = -> [View003]
  Rotation = 0
  ScaleType = 0
  TheoreticalExact = false
  Type = 2
  UnderTolerance = 0
  X = -77.5577
  Y = 23.2911
FEATURE [TechDraw::DrawViewDimension] Dimension059
  Arbitrary = false
  ArbitraryTolerances = false
  EqualTolerance = true
  FormatSpec = %.2f
  FormatSpecOverTolerance = %+.2f
  FormatSpecUnderTolerance = %+.2f
  Inverted = false
  LockPosition = false
  MeasureType = 1
  OverTolerance = 0
  References2D = -> [View003]
  Rotation = 0
  ScaleType = 0
  TheoreticalExact = false
  Type = 1
  UnderTolerance = 0
  X = 14.3759
  Y = 46.8661
FEATURE [TechDraw::DrawViewDimension] Dimension049
  Arbitrary = false
  ArbitraryTolerances = false
  EqualTolerance = true
  FormatSpec = %.2f
  FormatSpecOverTolerance = %+.2f
  FormatSpecUnderTolerance = %+.2f
  Inverted = false
  LockPosition = false
  MeasureType = 1
  OverTolerance = 0
  References2D = -> [View003]
  Rotation = 0
  ScaleType = 0
  TheoreticalExact = false
  Type = 1
  UnderTolerance = 0
  X = 6.80698
  Y = 58.0763
FEATURE [TechDraw::DrawViewDimension] Dimension051
  Arbitrary = false
  ArbitraryTolerances = false
  EqualTolerance = true
  FormatSpec = %.2f
  FormatSpecOverTolerance = %+.2f
  FormatSpecUnderTolerance = %+.2f
  Inverted = false
  LockPosition = false
  MeasureType = 1
  OverTolerance = 0
  References2D = -> [View003]
  Rotation = 0
  ScaleType = 0
  TheoreticalExact = false
  Type = 1
  UnderTolerance = 0
  X = -13.4458
  Y = 55.2167
FEATURE [TechDraw::DrawViewDimension] Dimension052
  Arbitrary = false
  ArbitraryTolerances = false
  EqualTolerance = true
  FormatSpec = %.2f
  FormatSpecOverTolerance = %+.2f
  FormatSpecUnderTolerance = %+.2f
  Inverted = false
  LockPosition = false
  MeasureType = 1
  OverTolerance = 0
  References2D = -> [View003]
  Rotation = 0
  ScaleType = 0
  TheoreticalExact = false
  Type = 2
  UnderTolerance = 0
  X = -87.0572
  Y = 12.8443
FEATURE [TechDraw::DrawViewDimension] Dimension055
  Arbitrary = false
  ArbitraryTolerances = false
  EqualTolerance = true
  FormatSpec = ⌀%.2f
  FormatSpecOverTolerance = %+.2f
  FormatSpecUnderTolerance = %+.2f
  Inverted = false
  LockPosition = false
  MeasureType = 1
  OverTolerance = 0
  References2D = -> [View003]
  Rotation = 0
  ScaleType = 0
  TheoreticalExact = false
  Type = 5
  UnderTolerance = 0
  X = 76.1875
  Y = 3.32696
FEATURE [TechDraw::DrawViewDimension] Dimension057
  Arbitrary = false
  ArbitraryTolerances = false
  EqualTolerance = true
  FormatSpec = ⌀%.2f
  FormatSpecOverTolerance = %+.2f
  FormatSpecUnderTolerance = %+.2f
  Inverted = false
  LockPosition = false
  MeasureType = 1
  OverTolerance = 0
  References2D = -> [View003]
  Rotation = 0
  ScaleType = 0
  TheoreticalExact = false
  Type = 5
  UnderTolerance = 0
  X = -64.2104
  Y = 57.8892
FEATURE [TechDraw::DrawViewDimension] Dimension060
  Arbitrary = false
  ArbitraryTolerances = false
  EqualTolerance = true
  FormatSpec = R%.2f
  FormatSpecOverTolerance = %+.2f
  FormatSpecUnderTolerance = %+.2f
  Inverted = false
  LockPosition = false
  MeasureType = 1
  OverTolerance = 0
  References2D = -> [View003]
  Rotation = 0
  ScaleType = 0
  TheoreticalExact = false
  Type = 4
  UnderTolerance = 0
  X = 73.1932
  Y = -33.6024
FEATURE [TechDraw::DrawViewDimension] Dimension062
  Arbitrary = false
  ArbitraryTolerances = false
  EqualTolerance = true
  FormatSpec = %.2f
  FormatSpecOverTolerance = %+.2f
  FormatSpecUnderTolerance = %+.2f
  Inverted = false
  LockPosition = false
  MeasureType = 1
  OverTolerance = 0
  References2D = -> [View003]
  Rotation = 0
  ScaleType = 0
  TheoreticalExact = false
  Type = 2
  UnderTolerance = 0
  X = -51.8526
  Y = -28.7166
FEATURE [TechDraw::DrawViewDimension] Dimension064
  Arbitrary = false
  ArbitraryTolerances = false
  EqualTolerance = true
  FormatSpec = %.2f
  FormatSpecOverTolerance = %+.2f
  FormatSpecUnderTolerance = %+.2f
  Inverted = false
  LockPosition = false
  MeasureType = 1
  OverTolerance = 0
  References2D = -> [View003]
  Rotation = 0
  ScaleType = 0
  TheoreticalExact = false
  Type = 1
  UnderTolerance = 0
  X = -37.3778
  Y = -20.7536
FEATURE [TechDraw::DrawViewDimension] Dimension061
  Arbitrary = false
  ArbitraryTolerances = false
  EqualTolerance = true
  FormatSpec = %.2f
  FormatSpecOverTolerance = %+.2f
  FormatSpecUnderTolerance = %+.2f
  Inverted = false
  LockPosition = false
  MeasureType = 1
  OverTolerance = 0
  References2D = -> [View003]
  Rotation = 0
  ScaleType = 0
  TheoreticalExact = false
  Type = 2
  UnderTolerance = 0
  X = -60.5558
  Y = -21.7249
FEATURE [TechDraw::DrawViewDimension] Dimension063
  Arbitrary = false
  ArbitraryTolerances = false
  EqualTolerance = true
  FormatSpec = %.2f
  FormatSpecOverTolerance = %+.2f
  FormatSpecUnderTolerance = %+.2f
  Inverted = false
  LockPosition = false
  MeasureType = 1
  OverTolerance = 0
  References2D = -> [View003]
  Rotation = 0
  ScaleType = 0
  TheoreticalExact = false
  Type = 1
  UnderTolerance = 0
  X = -36.0157
  Y = -32.5501
FEATURE [TechDraw::DrawViewDimension] Dimension065
  Arbitrary = false
  ArbitraryTolerances = false
  EqualTolerance = true
  FormatSpec = %.2f
  FormatSpecOverTolerance = %+.2f
  FormatSpecUnderTolerance = %+.2f
  Inverted = false
  LockPosition = false
  MeasureType = 1
  OverTolerance = 0
  References2D = -> [View003]
  Rotation = 0
  ScaleType = 0
  TheoreticalExact = false
  Type = 1
  UnderTolerance = 0
  X = -60.9058
  Y = -44.8128
FEATURE [TechDraw::DrawViewDimension] Dimension066
  Arbitrary = false
  ArbitraryTolerances = false
  EqualTolerance = true
  FormatSpec = %.2f
  FormatSpecOverTolerance = %+.2f
  FormatSpecUnderTolerance = %+.2f
  Inverted = false
  LockPosition = false
  MeasureType = 1
  OverTolerance = 0
  References2D = -> [View003]
  Rotation = 0
  ScaleType = 0
  TheoreticalExact = false
  Type = 1
  UnderTolerance = 0
  X = -3.36187
  Y = -31.2735
FEATURE [TechDraw::DrawPage] Page
  KeepUpdated = true
  NextBalloonIndex = 1
  ProjectionType = 0
  Template = -> Template
  Views = -> [View,View002,View003,View004,View005,Dimension,Dimension001,Dimension002,Dimension004,Dimension006,Dimension007,Dimension008,Dimension009,Dimension010,Dimension011,Dimension012,Dimension013,Dimension014,Dimension015,Dimension016,Dimension017,Dimension018,Dimension019,Dimension021,Dimension022,Dimension023,Dimension024,Dimension025,Dimension026,Dimension027,Dimension028,Dimension029,Dimension030,+36 more]
